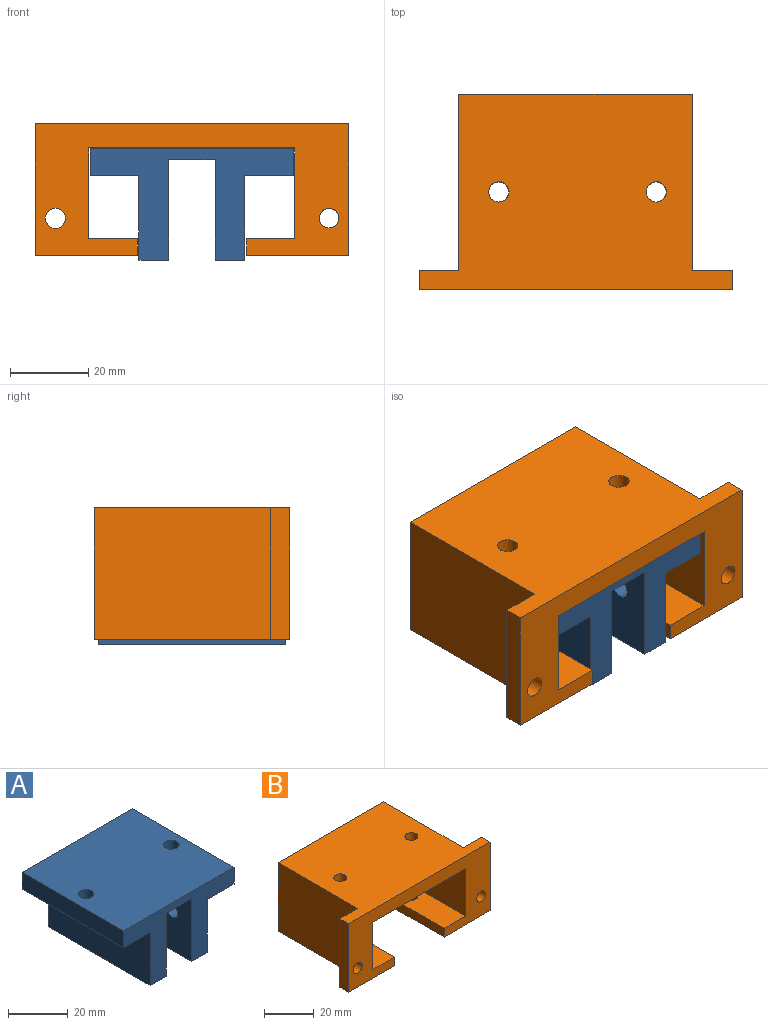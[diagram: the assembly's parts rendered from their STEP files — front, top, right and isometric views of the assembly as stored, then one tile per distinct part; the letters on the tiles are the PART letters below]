
ASSEMBLY  parts=2 mates=1
PART A: 20 faces, bbox 52.1x48x28.5 mm
  f0: plane 48x12.6mm, normal (0,0,-1), area 583.5mm2, adj f6,f7,f13,f18,f19
  f1: plane 48x12.46mm, normal (0,0,-1), area 577mm2, adj f2,f9,f12,f18,f19
  f2: plane 48x21.59mm, normal (-1,0,0), area 995.8mm2, adj f1,f10,f16,f17,f18,f19
  f3: plane 48x25.75mm, normal (1,0,0), area 1195.2mm2, adj f4,f10,f16,f17,f18,f19
  f4: plane 48x11.93mm, normal (0,0,-1), area 572.5mm2, adj f3,f5,f18,f19
  f5: plane 48x25.75mm, normal (-1,0,0), area 1195.2mm2, adj f4,f11,f14,f15,f18,f19
  f6: plane 48x21.59mm, normal (1,0,0), area 995.8mm2, adj f0,f11,f14,f15,f18,f19
  f7: plane 48x6.87mm, normal (1,0,0), area 329.8mm2, adj f0,f8,f18,f19
  f8: plane 52.13x48mm, normal (0,0,1), area 2459.9mm2, adj f7,f9,f12,f13,f18,f19
  f9: plane 48x6.87mm, normal (-1,0,0), area 329.8mm2, adj f1,f8,f18,f19
  f10: plane 48x7.57mm, normal (0,0,-1), area 363.5mm2, adj f2,f3,f18,f19
  f11: plane 48x7.57mm, normal (0,0,-1), area 363.5mm2, adj f5,f6,f18,f19
  f12: cylinder r=2.6mm len=6.87mm, axis (0,0,1), area 112.3mm2, adj f1,f8
  f13: cylinder r=2.6mm len=6.87mm, axis (0,0,1), area 112.3mm2, adj f0,f8
  f14: cylinder r=2.55mm len=7.57mm, axis (1,0,0), area 121.1mm2, adj f5,f6
  f15: cylinder r=2.55mm len=7.57mm, axis (1,0,0), area 121.1mm2, adj f5,f6
  f16: cylinder r=2.55mm len=7.57mm, axis (1,0,0), area 121.1mm2, adj f2,f3
  f17: cylinder r=2.55mm len=7.57mm, axis (1,0,0), area 121.1mm2, adj f2,f3
  f18: plane 52.13x28.47mm, normal (0,1,0), area 635.7mm2, adj f0,f1,f2,f3,f4,f5,f6,f7
  f19: plane 52.13x28.47mm, normal (0,-1,0), area 635.7mm2, adj f0,f1,f2,f3,f4,f5,f6,f7
PART B: 24 faces, bbox 80.2x50x33.6 mm
  f0: plane 50x26.04mm, normal (0,0,-1), area 816.1mm2, adj f1,f3,f13,f16,f17,f18,f23
  f1: plane 59.89x33.64mm, normal (0,1,0), area 668.5mm2, adj f0,f2,f4,f6,f7,f8,f9,f12
  f2: plane 50x12.3mm, normal (0,0,1), area 593.8mm2, adj f1,f8,f13,f18,f23
  f3: plane 33.64x4.93mm, normal (1,0,0), area 165.8mm2, adj f0,f4,f13,f16
  f4: plane 80.21x50mm, normal (0,0,1), area 3052.2mm2, adj f1,f3,f10,f13,f14,f15,f16,f17
  f5: cylinder r=2.5mm len=5mm, axis (0,-1,0), area 77.4mm2, adj f13,f16
  f6: plane 50x26.12mm, normal (0,0,-1), area 833.6mm2, adj f1,f10,f13,f14,f15,f19,f20
  f7: plane 52.8x50mm, normal (0,0,-1), area 2597.7mm2, adj f1,f8,f12,f13,f21,f22
  f8: plane 50x23.25mm, normal (-1,0,0), area 1162.6mm2, adj f1,f2,f7,f13
  f9: plane 50x12.45mm, normal (0,0,1), area 601.4mm2, adj f1,f12,f13,f19,f20
  f10: plane 33.64x4.93mm, normal (-1,0,0), area 165.8mm2, adj f4,f6,f13,f14
  f11: cylinder r=2.57mm len=5.13mm, axis (0,-1,0), area 79.4mm2, adj f13,f14
  f12: plane 50x23.25mm, normal (1,0,0), area 1162.6mm2, adj f1,f7,f9,f13
  f13: plane 80.21x33.64mm, normal (0,-1,0), area 1311.6mm2, adj f0,f2,f3,f4,f5,f6,f7,f8
  f14: plane 33.64x10.01mm, normal (0,1,0), area 316.1mm2, adj f4,f6,f10,f11,f15
  f15: plane 45.07x33.64mm, normal (-1,0,0), area 1516.2mm2, adj f1,f4,f6,f14
  f16: plane 33.64x10.31mm, normal (0,1,0), area 327mm2, adj f0,f3,f4,f5,f17
  f17: plane 45.07x33.64mm, normal (1,0,0), area 1516.2mm2, adj f0,f1,f4,f16
  f18: plane 50x4.22mm, normal (-1,0,0), area 211.1mm2, adj f0,f1,f2,f13
  f19: plane 50x4.22mm, normal (1,0,0), area 211.1mm2, adj f1,f6,f9,f13
  f20: cylinder r=2.6mm len=5.2mm, axis (0,0,1), area 69mm2, adj f6,f9
  f21: cylinder r=2.6mm len=6.17mm, axis (0,0,1), area 100.7mm2, adj f4,f7
  f22: cylinder r=2.6mm len=6.17mm, axis (0,0,1), area 100.7mm2, adj f4,f7
  f23: cylinder r=2.6mm len=5.2mm, axis (0,0,1), area 69mm2, adj f0,f2
PLACE A t=(34.97,-7.62,18.32)mm
PLACE B t=(34.99,-7.62,12.75)mm fixed
MATE slider B.f7 <-> A.f4  axis (0,0,-1) through (6.67,17.38,18.56)mm
